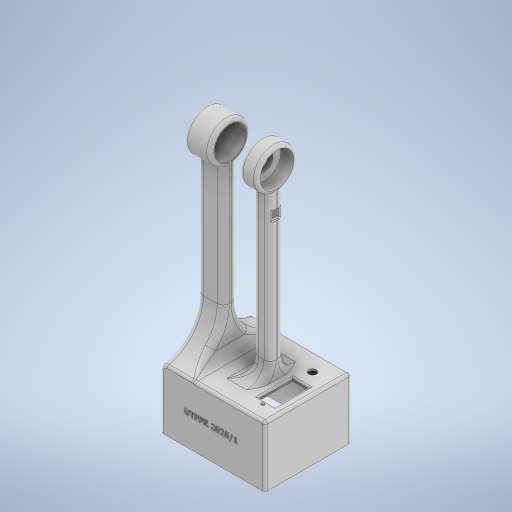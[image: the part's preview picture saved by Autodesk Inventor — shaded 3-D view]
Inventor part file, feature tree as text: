
AUTODESK INVENTOR PART (.ipt)
format: ipt  version: 2024.1 (Build 281209000, 209)  size: 2,012,672 bytes
history: native  units: mm
features: sketch x57, extrude x46, fillet x18, other x13
ambient origin geometry x8: Origin, YZ Plane, XZ Plane, XY Plane, X Axis, Y Axis, Z Axis, Center Point
bodies: Body1 (feature_tree), Body2 (feature_tree), Body3 (feature_tree)
feature tree (134):
  other  "Sólido1"
  sketch  "Esboço1"  dims[d2=40.0mm d3=100.0mm]
  extrude  "Extrusão1"  Depth=100.0mm
  extrude  "Extrusão2"  Depth=120.0mm
  extrude  "Extrusão3"  Depth=10.0mm
  extrude  "Extrusão4"  Depth=39.0mm
  extrude  "Extrusão5"  Depth=9.5mm
  extrude  "Extrusão6"  Depth=5.0mm
  extrude  "Extrusão7"  Depth=5.0mm
  extrude  "Extrusão16"  Depth=70.0mm
  sketch  "Esboço19"  dims[d30=75.0mm d31=200.0mm d32=0.0mm]
  extrude  "Extrusão17"  Depth=50.0mm
  extrude  "Extrusão19"  Depth=200.0mm TaperAngle=0.0deg
  sketch  "Esboço23"  dims[d37=1.0mm d38=39.0mm]
  extrude  "Extrusão20"  Depth=23.0mm
  extrude  "Extrusão21"  Depth=19.25mm
  extrude  "Extrusão22"  Depth=1.0mm
  extrude  "Extrusão23"  Depth=5.0mm
  extrude  "Extrusão24"  Depth=200.0mm TaperAngle=0.0deg
  extrude  "Extrusão25"  Depth=30.0mm TaperAngle=0.0deg
  extrude  "Extrusão26"  Depth=6.0mm
  sketch  "Esboço31"  dims[d102=10.0mm d103=0.0mm d104=10.0mm d105=0.0mm]
  extrude  "Extrusão27"  Depth=5.0mm TaperAngle=0.0deg
  extrude  "Extrusão28"  Depth=5.0mm
  extrude  "Extrusão29"  Depth=1.0mm
  extrude  "Extrusão30"  Depth=10.0mm TaperAngle=0.0deg
  extrude  "Extrusão31"  Depth=5.0mm TaperAngle=0.0deg
  fillet  "Arredondamento23"  Radius=15.0mm
  fillet  "Arredondamento24"  Radius=5.0mm
  fillet  "Arredondamento25"  Radius=3.0mm
  sketch  "Esboço38"  dims[d123=110.0mm d124=100.0mm d125=0.0mm]
  extrude  "Extrusão32"  Depth=6.0mm
  extrude  "Extrusão33"  Depth=6.0mm
  extrude  "Extrusão34"  Depth=6.0mm TaperAngle=0.0deg
  extrude  "Extrusão35"  Depth=110.0mm
  extrude  "Extrusão36"  Depth=100.0mm TaperAngle=0.0deg
  extrude  "Extrusão37"  Depth=0.5mm
  sketch  "Esboço45"  dims[d153=45.0mm d154=0.0mm d155=10.0mm d156=0.0mm]
  extrude  "Extrusão38"  Depth=10.0mm TaperAngle=0.0deg
  extrude  "Extrusão39"  Depth=10.0mm
  extrude  "Extrusão40"  Depth=3.0mm
  extrude  "Extrusão41"  Depth=10.0mm TaperAngle=0.0deg
  extrude  "Extrusão42"  Depth=5.0mm
  extrude  "Extrusão43"  Depth=10.0mm TaperAngle=0.0deg
  extrude  "Extrusão44"  Depth=5.0mm TaperAngle=0.0deg
  extrude  "Extrusão45"  Depth=13.0mm
  sketch  "Esboço54"  dims[d188=4.0mm d189=1.0mm]
  sketch  "Esboço55"  dims[d190=3.0mm d191=4.0mm]
  sketch  "Esboço56"  dims[d192=66.0mm d193=0.0mm d194=30.0mm d195=5.0mm d196=10.0mm d197=3.0mm d198=3.0mm d199=210.0mm d200=0.0mm d201=6.0mm]
  sketch  "Esboço57"  dims[d202=300.0mm d203=0.0mm d204=3.0mm]
  extrude  "Extrusão46"  Depth=5.0mm
  extrude  "Extrusão47"  Depth=120.0mm TaperAngle=0.0deg
  sketch  "Esboço60"  dims[d208=36.5mm]
  extrude  "Extrusão48"  Depth=66.0mm TaperAngle=0.0deg
  extrude  "Extrusão49"  Depth=66.0mm TaperAngle=0.0deg
  extrude  "Extrusão50"  Depth=43.0mm
  extrude  "Extrusão51"  Depth=10.0mm
  fillet  "Arredondamento26"  Radius=10.0mm
  fillet  "Arredondamento27"  Radius=22.0mm
  fillet  "Arredondamento28"  Radius=19.0mm
  fillet  "Arredondamento29"  Radius=39.0mm
  fillet  "Arredondamento30"  Radius=23.0mm
  fillet  "Arredondamento31"  Radius=22.0mm
  fillet  "Arredondamento32"  Radius=9.0mm
  fillet  "Arredondamento33"  Radius=66.0mm
  fillet  "Arredondamento34"  Radius=9.5mm
  extrude  "Extrusão52"  Depth=1.0mm
  extrude  "Extrusão53"  Depth=4.0mm
  extrude  "Extrusão54"  Depth=6.0mm
  fillet  "Arredondamento35"  Radius=5.0mm
  fillet  "Arredondamento36"  Radius=10.0mm
  fillet  "Arredondamento37"  Radius=3.0mm
  fillet  "Arredondamento38"  Radius=3.0mm
  fillet  "Arredondamento39"  Radius=210.0mm
  fillet  "Arredondamento40"  Radius=6.0mm
  extrude  "Extrusão55"  Depth=3.0mm
  sketch  "Esboço2"  dims[d4=60.0mm d5=120.0mm]
  sketch  "Esboço3"  dims[d6=30.0mm d7=0.0mm d8=10.0mm]
  sketch  "Esboço4"  dims[d9=28.0mm d10=39.0mm]
  sketch  "Esboço5"  dims[d11=19.0mm d12=9.5mm]
  sketch  "Esboço6"  dims[d19=30.0mm d20=0.0mm d21=5.0mm]
  sketch  "Esboço7"  dims[d22=5.0mm d23=70.0mm]
  sketch  "Esboço8"  dims[d24=110.0mm d25=70.0mm]
  sketch  "Esboço18"  dims[d26=25.0mm d27=0.0mm d28=50.0mm]
  sketch  "Esboço20"  dims[d33=150.0mm d34=23.0mm]
  sketch  "Esboço22"  dims[d35=36.5mm d36=19.25mm]
  sketch  "Esboço24"  dims[d39=200.0mm d40=0.0mm d41=5.0mm]
  sketch  "Esboço25"  dims[d44=46.0mm d45=200.0mm d46=0.0mm]
  other  "Contorno projetado1"
  sketch  "Esboço26"  dims[d49=8.5mm d50=30.0mm d51=0.0mm]
  sketch  "Esboço27"  dims[d87=6.0mm d88=0.0mm d90=8.5mm]
  sketch  "Esboço28"  dims[d91=20.5mm d92=5.0mm d93=0.0mm]
  sketch  "Esboço29"  dims[d97=8.0mm d98=0.0mm d99=5.0mm]
  sketch  "Esboço30"  dims[d100=6.0mm d101=1.0mm]
  sketch  "Esboço32"  dims[d106=70.0mm d107=8.0mm d108=0.0mm d109=15.0mm d110=0.0mm d111=5.0mm d112=3.0mm]
  other  "Contorno projetado2"
  other  "Sólido2"
  sketch  "Esboço33"  dims[d113=6.0mm d114=3.0mm]
  other  "Contorno projetado3"
  sketch  "Esboço34"  dims[d115=6.0mm d116=6.0mm]
  other  "Contorno projetado4"
  sketch  "Esboço35"  dims[d117=6.0mm d118=60.0mm d119=0.0mm]
  other  "Contorno projetado5"
  other  "Contorno projetado6"
  sketch  "Esboço36"  dims[d120=60.0mm d121=0.0mm d122=110.0mm]
  other  "Contorno projetado7"
  other  "Contorno projetado8"
  sketch  "Esboço39"  dims[d139=9.0mm d140=0.5mm]
  sketch  "Esboço40"  dims[d141=3.0mm d142=10.0mm d143=0.0mm]
  other  "Contorno projetado9"
  other  "Sólido3"
  sketch  "Esboço41"  dims[d144=10.0mm d145=3.0mm]
  other  "Contorno projetado10"
  sketch  "Esboço42"  dims[d146=3.0mm d147=3.0mm]
  sketch  "Esboço43"  dims[d148=3.0mm d149=10.0mm d150=0.0mm]
  sketch  "Esboço44"  dims[d151=10.0mm d152=5.0mm]
  sketch  "Esboço46"  dims[d157=1.0mm d158=5.0mm d159=0.0mm]
  sketch  "Esboço47"  dims[d160=2.0mm d161=13.0mm]
  sketch  "Esboço48"  dims[d162=5.0mm d163=100.0mm]
  sketch  "Esboço49"  dims[d164=70.0mm d165=120.0mm d166=0.0mm]
  sketch  "Esboço50"  dims[d167=2.0mm d168=66.0mm d169=0.0mm]
  sketch  "Esboço51"  dims[d170=2.0mm d171=66.0mm d172=0.0mm]
  sketch  "Esboço52"  dims[d174=30.0mm d175=43.0mm]
  sketch  "Esboço53"  dims[d176=5.0mm d177=18.0mm d178=10.0mm d179=22.0mm d180=19.0mm d181=39.0mm d182=23.0mm d183=22.0mm d184=9.0mm d185=66.0mm d186=0.0mm d187=9.5mm]
  sketch  "Esboço58"  dims[d205=5.0mm]
  sketch  "Esboço59"  dims[d206=300.0mm d207=0.0mm]
  sketch  "Esboço61"  dims[d209=5.0mm]
  sketch  "Esboço62"  dims[d210=10.0mm d211=0.0mm]
  sketch  "Esboço63"  dims[d212=60.0mm d213=0.0mm]
  sketch  "Esboço64"  dims[d214=5.0mm]
  sketch  "Esboço65"  dims[d215=60.0mm d216=0.0mm]
  sketch  "Esboço66"  dims[d217=17.0mm]
  sketch  "Esboço67"  dims[d218=13.0mm]
  sketch  "Esboço68"  dims[d219=2.0mm d220=15.0mm d221=8.0mm d222=16.0mm d223=20.0mm d224=220.0mm d225=0.0mm d226=34.5mm d227=220.0mm d228=0.0mm d229=10.0mm d230=0.0mm d231=34.5mm d232=10.0mm d233=0.0mm d234=39.0mm d235=10.0mm d236=0.0mm d237=20.5mm d238=5.0mm d239=0.0mm d240=15.0mm d241=2.0mm d242=4.0mm d243=4.0mm d244=4.0mm d245=15.0mm d246=0.0mm d247=160.0mm d248=5.0mm d249=0.0mm d250=5.0mm d251=0.0mm d252=50.0mm d253=20.0mm d254=10.0mm d255=7.0mm d256=7.0mm d257=4.0mm d258=2.0mm d259=3.0mm d260=3.0mm d261=1.0mm d262=0.0mm d263=1.0mm d264=0.0mm d265=9.0mm d266=9.0mm d267=18.0mm d268=18.0mm d269=18.0mm d270=2.0mm d271=0.0mm d272=3.0mm d273=3.0mm d274=3.0mm d275=1.0mm d276=4.0mm d277=1.0mm d278=500.0mm d279=0.0mm d63=0.5mm d64=0.872665mm d65=0.5mm d66=0.872665mm d173=0.5mm]
